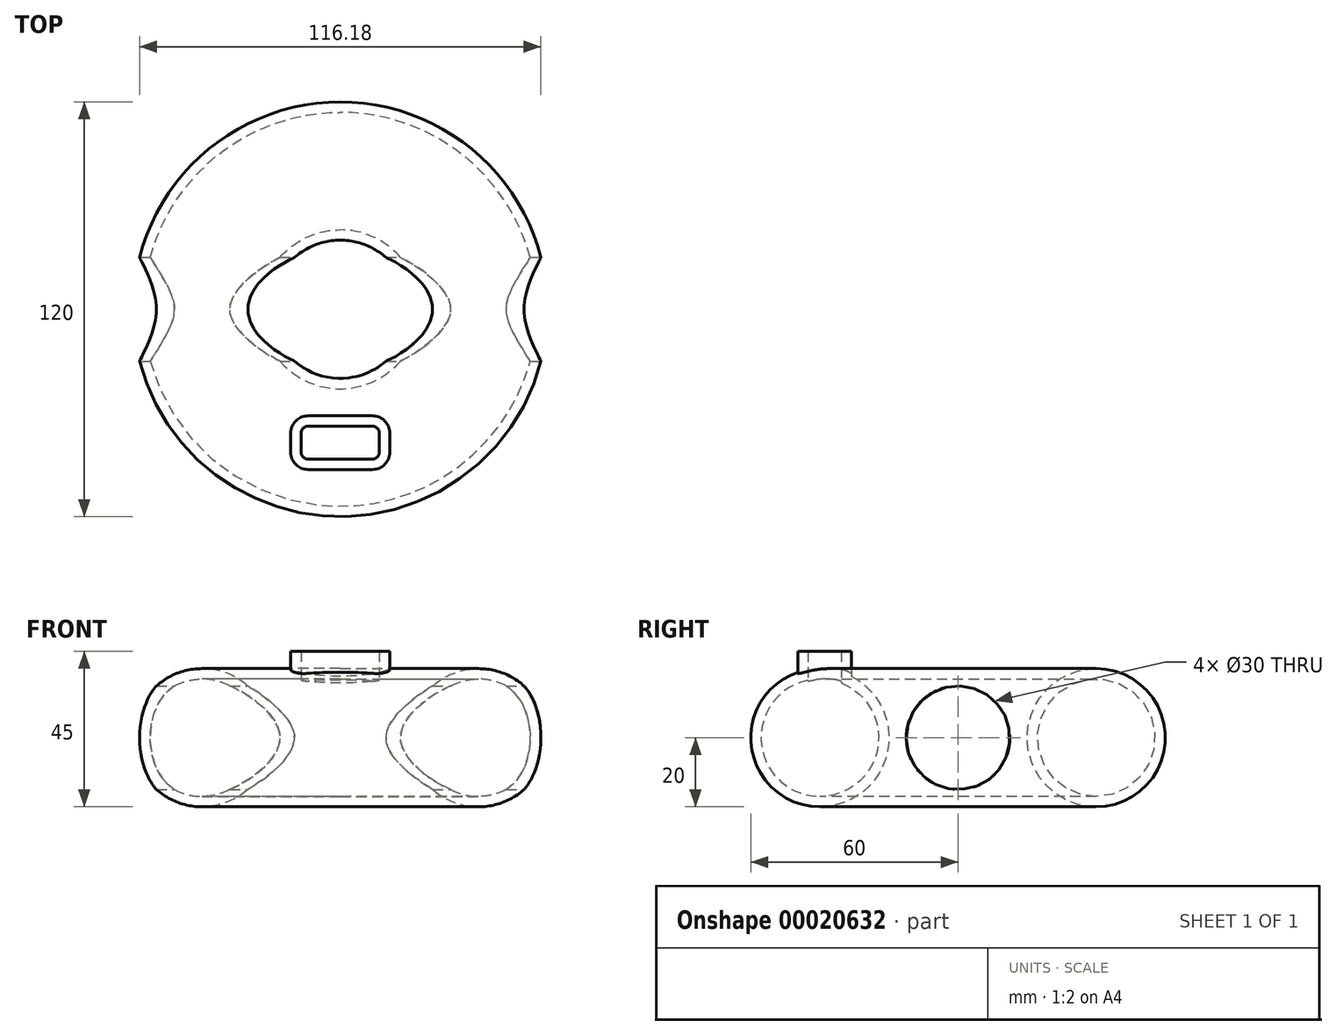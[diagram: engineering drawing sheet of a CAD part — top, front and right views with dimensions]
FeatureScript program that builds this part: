
annotation { "Feature Type Name" : "Feature", "Feature Type Description" : "" }
export const myFeature = defineFeature(function(context is Context, id is Id, definition is map)
    precondition{}
    {
        {
            var Q0;
            Q0=qCreatedBy(makeId("Front.planeOp"),FACE);
            var sketch = newSketch(context, id + "F0", { "sketchPlane" : qUnion([Q0])});
            skCircle(sketch, "E0", {"center": v(-40, 0) * mm, "radius": 20 * mm});
            skLineSegment(sketch, "E1", {"start": v(0, 0) * mm, "end": v(0, 24.26) * mm, "construction": true});
            skSolve(sketch);
        }
        {
            var Q0;
            Q0 = qSketchRegion(id + "F0", true);
            var Q1;
            Q1=sQuery(id+"F0.wireOp",EDGE,"E1");
            revolve(context, id + "F1", {"entities" : qUnion([Q0]), "axis" : qUnion([Q1]), "revolveType" : RevolveType.FULL});
        }
        {
            var Q0;
            Q0=qCreatedBy(makeId("Right.planeOp"),FACE);
            var sketch = newSketch(context, id + "F2", { "sketchPlane" : qUnion([Q0])});
            skCircle(sketch, "E2", {"center": v(0, 0) * mm, "radius": 15 * mm});
            skSolve(sketch);
        }
        {
            var Q0;
            Q0=qCreatedBy(makeId("Top.planeOp"),FACE);
            var sketch = newSketch(context, id + "F3", { "sketchPlane" : qUnion([Q0])});
            skLineSegment(sketch, "E3.rect.bottom", {"start": v(9.33, -30.84) * mm, "end": v(-9.33, -30.84) * mm});
            skLineSegment(sketch, "E3.rect.top", {"start": v(9.33, -46.37) * mm, "end": v(-9.33, -46.37) * mm});
            skLineSegment(sketch, "E3.rect.left", {"start": v(14.33, -35.84) * mm, "end": v(14.33, -41.37) * mm});
            skLineSegment(sketch, "E3.rect.right", {"start": v(-14.33, -35.84) * mm, "end": v(-14.33, -41.37) * mm});
            skPoint(sketch, "E3.rect.middle", {"position": v(0, -38.6) * mm});
            skPoint(sketch, "E4.visualSharp", {"position": v(-14.33, -30.84) * mm});
            skArc(sketch, "E4.filletArc", {"start": v(-9.33, -30.84) * mm, "mid": v(-12.86, -32.3) * mm, "end": v(-14.33, -35.84) * mm});
            skPoint(sketch, "E5.visualSharp", {"position": v(-14.33, -46.37) * mm});
            skArc(sketch, "E5.filletArc", {"start": v(-14.33, -41.37) * mm, "mid": v(-12.86, -44.91) * mm, "end": v(-9.33, -46.37) * mm});
            skPoint(sketch, "E6.visualSharp", {"position": v(14.33, -46.37) * mm});
            skArc(sketch, "E6.filletArc", {"start": v(9.33, -46.37) * mm, "mid": v(12.86, -44.91) * mm, "end": v(14.33, -41.37) * mm});
            skPoint(sketch, "E7.visualSharp", {"position": v(14.33, -30.84) * mm});
            skArc(sketch, "E7.filletArc", {"start": v(14.33, -35.84) * mm, "mid": v(12.86, -32.3) * mm, "end": v(9.33, -30.84) * mm});
            skSolve(sketch);
        }
        {
            var Q0;
            Q0 = qSketchRegion(id + "F3", true);
            extrude(context, id + "F4", {"entities" : qUnion([Q0]), "operationType" : NewBodyOperationType.ADD, "depth" : 25 * mm});
        }
        {
            var Q0;
            Q0=makeQuery(id+"F4.opExtrude","CAP_FACE",FACE,{"disambiguationData":[OSD([sQuery(id+"F3.wireOp",EDGE,"E3.rect.bottom"),sQuery(id+"F3.wireOp",EDGE,"E3.rect.top"),sQuery(id+"F3.wireOp",EDGE,"E3.rect.left"),sQuery(id+"F3.wireOp",EDGE,"E3.rect.right"),sQuery(id+"F3.wireOp",EDGE,"E4.filletArc"),sQuery(id+"F3.wireOp",EDGE,"E5.filletArc"),sQuery(id+"F3.wireOp",EDGE,"E6.filletArc"),sQuery(id+"F3.wireOp",EDGE,"E7.filletArc")])],"isStart":false});
            shell(context, id + "F5", {"entities" : qUnion([Q0]), "thickness" : 3 * mm});
        }
        {
            var Q0;
            Q0 = qSketchRegion(id + "F2", true);
            extrude(context, id + "F6", {"entities" : qUnion([Q0]), "operationType" : NewBodyOperationType.REMOVE, "endBound" : BoundingType.THROUGH_ALL, "oppositeDirection" : true, "depth" : 25 * mm, "hasSecondDirection" : true, "secondDirectionBound" : SecondDirectionBoundingType.THROUGH_ALL, "secondDirectionOppositeDirection" : false, "secondDirectionDepth" : 25 * mm});
        }
    });
